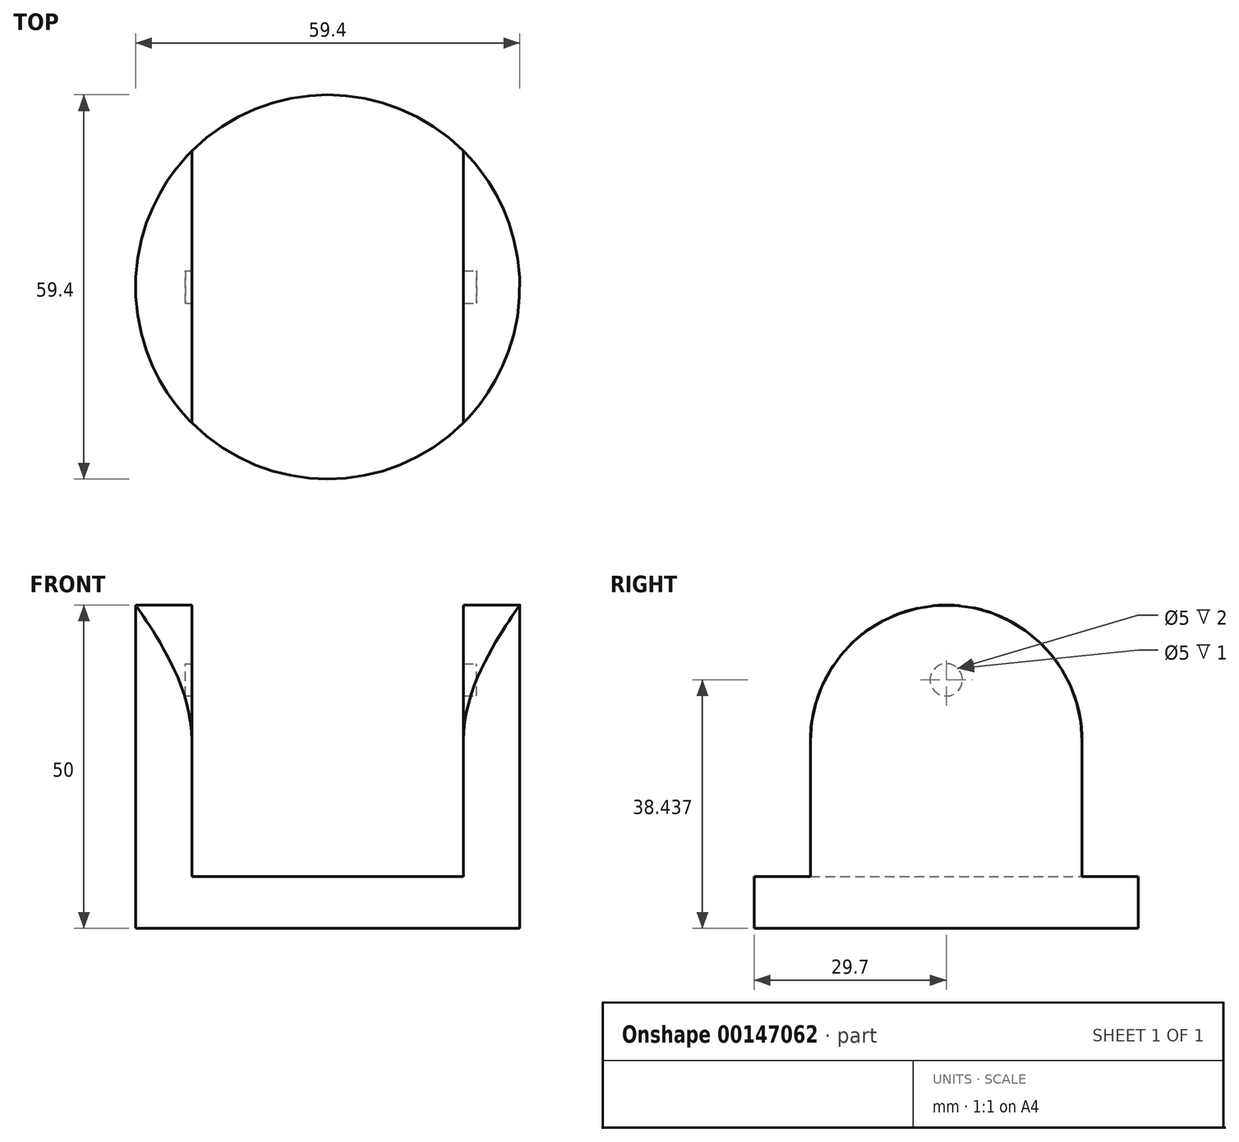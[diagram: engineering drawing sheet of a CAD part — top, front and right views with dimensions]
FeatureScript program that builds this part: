
annotation { "Feature Type Name" : "Feature", "Feature Type Description" : "" }
export const myFeature = defineFeature(function(context is Context, id is Id, definition is map)
    precondition{}
    {
        {
            var Q0;
            Q0=qCreatedBy(makeId("Top.planeOp"),FACE);
            var sketch = newSketch(context, id + "F0", { "sketchPlane" : qUnion([Q0])});
            skCircle(sketch, "E0", {"center": v(0, 0) * mm, "radius": 29.7 * mm});
            skLineSegment(sketch, "E1.bottom", {"start": v(21, 21) * mm, "end": v(-21, 21) * mm});
            skLineSegment(sketch, "E1.top", {"start": v(21, -21) * mm, "end": v(-21, -21) * mm});
            skLineSegment(sketch, "E1.left", {"start": v(21, 21) * mm, "end": v(21, -21) * mm});
            skLineSegment(sketch, "E1.right", {"start": v(-21, 21) * mm, "end": v(-21, -21) * mm});
            skSolve(sketch);
        }
        {
            var Q0;
            {var subQ0=sQuery(id+"F0.wireOp",EDGE,"E1.right");Q0=makeQuery(id+"F0.imprint","IMPRINT",FACE,{"disambiguationData":[TD([[makeQuery(id+"F0.imprint","IMPRINT",EDGE,{"derivedFrom":subQ0}),-1.0]])]});}
            var Q1;
            Q1=makeQuery(id+"F0.imprint","IMPRINT",FACE,{"disambiguationData":[TD([[makeQuery(id+"F0.imprint","IMPRINT",EDGE,{"derivedFrom":sQuery(id+"F0.wireOp",EDGE,"E1.bottom")}),1.0]])]});
            var Q2;
            {var subQ0=sQuery(id+"F0.wireOp",EDGE,"E1.bottom");Q2=makeQuery(id+"F0.imprint","IMPRINT",FACE,{"disambiguationData":[TD([[makeQuery(id+"F0.imprint","IMPRINT",EDGE,{"derivedFrom":subQ0}),-1.0]])]});}
            var Q3;
            {var subQ0=sQuery(id+"F0.wireOp",EDGE,"E1.left");Q3=makeQuery(id+"F0.imprint","IMPRINT",FACE,{"disambiguationData":[TD([[makeQuery(id+"F0.imprint","IMPRINT",EDGE,{"derivedFrom":subQ0}),1.0]])]});}
            var Q4;
            {var subQ0=sQuery(id+"F0.wireOp",EDGE,"E1.top");Q4=makeQuery(id+"F0.imprint","IMPRINT",FACE,{"disambiguationData":[TD([[makeQuery(id+"F0.imprint","IMPRINT",EDGE,{"derivedFrom":subQ0}),1.0]])]});}
            extrude(context, id + "F1", {"entities" : qUnion([Q0, Q1, Q2, Q3, Q4]), "depth" : 8 * mm});
        }
        {
            var Q0;
            {var subQ0=sQuery(id+"F0.wireOp",EDGE,"E1.right");Q0=makeQuery(id+"F0.imprint","IMPRINT",FACE,{"disambiguationData":[TD([[makeQuery(id+"F0.imprint","IMPRINT",EDGE,{"derivedFrom":subQ0}),-1.0]])]});}
            var Q1;
            {var subQ0=sQuery(id+"F0.wireOp",EDGE,"E1.left");Q1=makeQuery(id+"F0.imprint","IMPRINT",FACE,{"disambiguationData":[TD([[makeQuery(id+"F0.imprint","IMPRINT",EDGE,{"derivedFrom":subQ0}),1.0]])]});}
            extrude(context, id + "F2", {"entities" : qUnion([Q0, Q1]), "operationType" : NewBodyOperationType.ADD, "depth" : 50 * mm});
        }
        {
            var Q0;
            Q0=qCreatedBy(makeId("Right.planeOp"),FACE);
            var sketch = newSketch(context, id + "F3", { "sketchPlane" : qUnion([Q0])});
            skLineSegment(sketch, "E2.0", {"start": v(-21, 50) * mm, "end": v(-21, 8) * mm});
            skLineSegment(sketch, "E2.1", {"start": v(-21, 50) * mm, "end": v(21, 50) * mm});
            skLineSegment(sketch, "E2.2", {"start": v(21, 50) * mm, "end": v(21, 8) * mm});
            skLineSegment(sketch, "E3", {"start": v(-21, 29) * mm, "end": v(21, 29) * mm});
            skPoint(sketch, "E3.endSnap0", {"position": v(21, 29) * mm});
            skArc(sketch, "E4", {"start": v(-21, 29) * mm, "mid": v(0, 50) * mm, "end": v(21, 29) * mm});
            skCircle(sketch, "E5", {"center": v(0, 29) * mm, "radius": 3 * mm});
            skLineSegment(sketch, "E6.bottom", {"start": v(2.18, 31.06) * mm, "end": v(-2.18, 31.06) * mm});
            skLineSegment(sketch, "E6.top", {"start": v(2.18, 26.94) * mm, "end": v(-2.18, 26.94) * mm});
            skLineSegment(sketch, "E6.left", {"start": v(2.18, 31.06) * mm, "end": v(2.18, 26.94) * mm});
            skLineSegment(sketch, "E6.right", {"start": v(-2.18, 31.06) * mm, "end": v(-2.18, 26.94) * mm});
            skSolve(sketch);
        }
        {
            var Q0;
            {var subQ0=sQuery(id+"F3.wireOp",EDGE,"E2.1");var subQ1=sQuery(id+"F3.wireOp",EDGE,"E2.0");var subQ2=makeQuery(id+"F3.imprint","INTERSECT",VERTEX,{"derivedFrom":[subQ1,subQ0]});Q0=makeQuery(id+"F3.imprint","IMPRINT",FACE,{"disambiguationData":[TD([[makeQuery(id+"F3.imprint","IMPRINT",EDGE,{"disambiguationData":[TD([[subQ2,-1.0]])],"derivedFrom":subQ0}),-1.0]])]});}
            var Q1;
            {var subQ0=sQuery(id+"F3.wireOp",EDGE,"E2.2");var subQ1=sQuery(id+"F3.wireOp",EDGE,"E2.1");var subQ2=makeQuery(id+"F3.imprint","INTERSECT",VERTEX,{"derivedFrom":[subQ1,subQ0]});Q1=makeQuery(id+"F3.imprint","IMPRINT",FACE,{"disambiguationData":[TD([[makeQuery(id+"F3.imprint","IMPRINT",EDGE,{"disambiguationData":[TD([[subQ2,1.0]])],"derivedFrom":subQ1}),-1.0]])]});}
            extrude(context, id + "F4", {"entities" : qUnion([Q0, Q1]), "operationType" : NewBodyOperationType.REMOVE, "endBound" : BoundingType.SYMMETRIC, "oppositeDirection" : true, "depth" : 125.5 * mm});
        }
        {
            var Q0;
            Q0=makeQuery(id+"F2.opExtrude","SWEPT_FACE",FACE,{"disambiguationData":[OSD([sQuery(id+"F0.wireOp",EDGE,"E1.right")])]});
            var sketch = newSketch(context, id + "F5", { "sketchPlane" : qUnion([Q0])});
            skCircle(sketch, "E7", {"center": v(0, 75.67) * mm, "radius": 2.5 * mm});
            skCircle(sketch, "E8", {"center": v(0, 38.44) * mm, "radius": 2.5 * mm});
            skSolve(sketch);
        }
        {
            var Q0;
            Q0=makeQuery(id+"F5.imprint","IMPRINT",FACE,{"disambiguationData":[TD([[makeQuery(id+"F5.imprint","IMPRINT",EDGE,{"derivedFrom":sQuery(id+"F5.wireOp",EDGE,"E8")}),1.0]])]});
            extrude(context, id + "F6", {"entities" : qUnion([Q0]), "operationType" : NewBodyOperationType.REMOVE, "oppositeDirection" : true, "depth" : 1 * mm, "hasSecondDirection" : true, "secondDirectionOppositeDirection" : false, "secondDirectionDepth" : 44 * mm});
        }
    });
